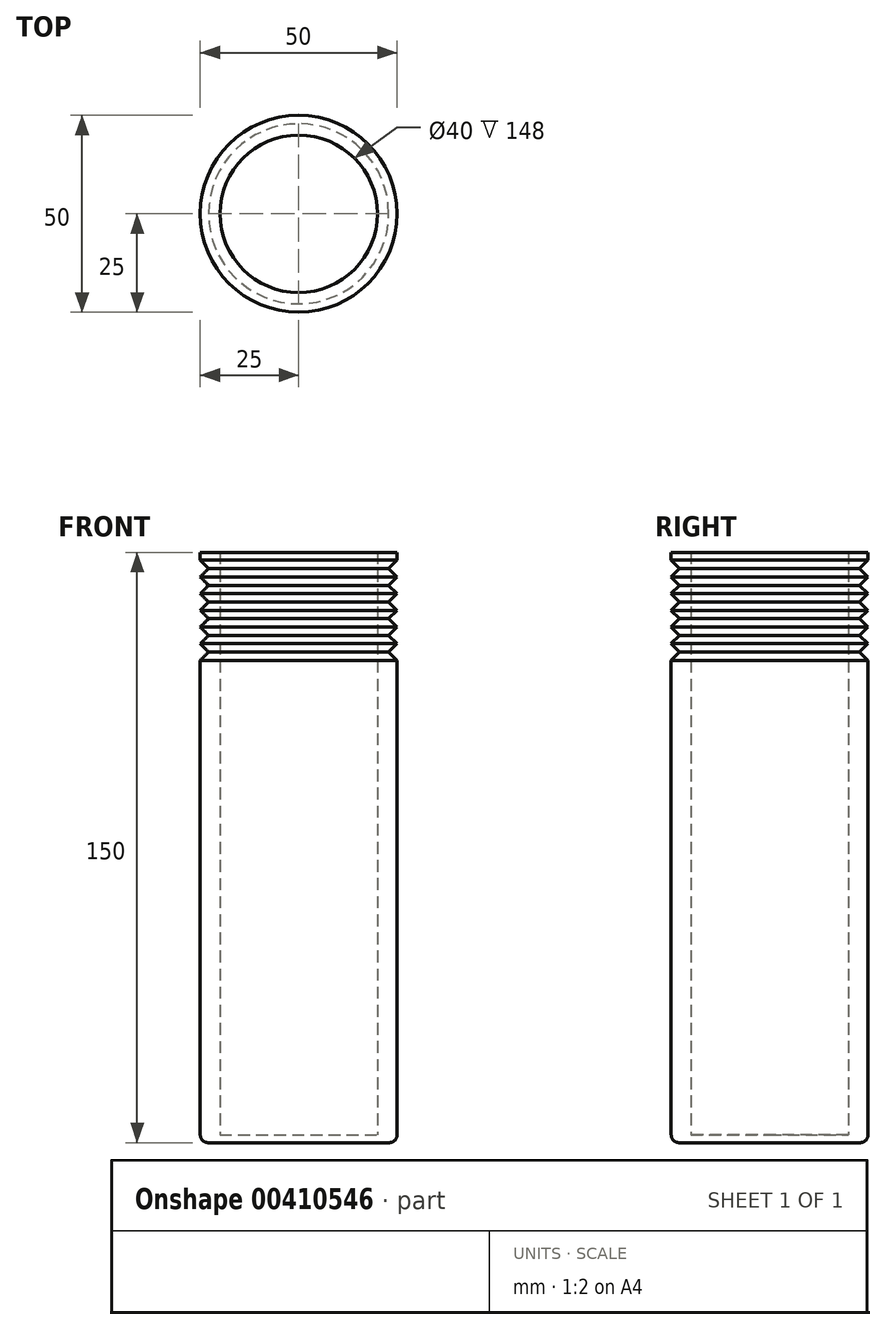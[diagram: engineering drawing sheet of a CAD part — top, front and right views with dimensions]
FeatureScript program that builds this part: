
annotation { "Feature Type Name" : "Feature", "Feature Type Description" : "" }
export const myFeature = defineFeature(function(context is Context, id is Id, definition is map)
    precondition{}
    {
        {
            var Q0;
            Q0=qCreatedBy(makeId("Front.planeOp"),FACE);
            var sketch = newSketch(context, id + "F0", { "sketchPlane" : qUnion([Q0])});
            skLineSegment(sketch, "E0", {"start": v(0, 0) * mm, "end": v(25, 0) * mm});
            skLineSegment(sketch, "E1", {"start": v(25, 0) * mm, "end": v(25, 122.52) * mm});
            skLineSegment(sketch, "E2", {"start": v(25, 150) * mm, "end": v(20, 150) * mm});
            skLineSegment(sketch, "E3", {"start": v(20, 150) * mm, "end": v(20, 2) * mm});
            skLineSegment(sketch, "E4", {"start": v(20, 2) * mm, "end": v(0, 2) * mm});
            skLineSegment(sketch, "E5", {"start": v(0, 2) * mm, "end": v(0, 0) * mm});
            skLineSegment(sketch, "E6", {"start": v(0, 2) * mm, "end": v(0, 245.04) * mm, "construction": true});
            skLineSegment(sketch, "E7", {"start": v(25, 147.98) * mm, "end": v(22.88, 145.86) * mm});
            skLineSegment(sketch, "E8", {"start": v(22.88, 145.86) * mm, "end": v(25, 143.74) * mm});
            skLineSegment(sketch, "E9", {"start": v(25, 143.74) * mm, "end": v(22.88, 141.62) * mm});
            skLineSegment(sketch, "E10", {"start": v(22.88, 141.62) * mm, "end": v(25, 139.5) * mm});
            skLineSegment(sketch, "E11", {"start": v(25, 139.5) * mm, "end": v(22.88, 137.37) * mm});
            skLineSegment(sketch, "E12", {"start": v(22.88, 137.37) * mm, "end": v(25, 135.25) * mm});
            skLineSegment(sketch, "E13", {"start": v(25, 135.25) * mm, "end": v(22.88, 133.13) * mm});
            skLineSegment(sketch, "E14", {"start": v(22.88, 133.13) * mm, "end": v(25, 131) * mm});
            skLineSegment(sketch, "E15", {"start": v(25, 131) * mm, "end": v(22.88, 128.89) * mm});
            skLineSegment(sketch, "E16", {"start": v(22.88, 128.89) * mm, "end": v(25, 126.77) * mm});
            skLineSegment(sketch, "E17", {"start": v(25, 126.77) * mm, "end": v(22.88, 124.64) * mm});
            skLineSegment(sketch, "E18", {"start": v(22.88, 124.64) * mm, "end": v(25, 122.52) * mm});
            skLineSegment(sketch, "E19.trimOffspring", {"start": v(25, 147.98) * mm, "end": v(25, 150) * mm});
            skSolve(sketch);
        }
        {
            var Q0;
            Q0 = qSketchRegion(id + "F0", true);
            var Q1;
            Q1=sQuery(id+"F0.wireOp",EDGE,"E6");
            revolve(context, id + "F1", {"entities" : qUnion([Q0]), "axis" : qUnion([Q1]), "revolveType" : RevolveType.FULL});
        }
        {
            var Q0;
            Q0=makeQuery(id+"F1.opRevolve","SWEPT_EDGE",EDGE,{"disambiguationData":[OSD([sQuery(id+"F0.wireOp",EDGE,"E0"),sQuery(id+"F0.wireOp",EDGE,"E1")])]});
            fillet(context, id + "F2", {"entities" : qUnion([Q0]), "radius" : 2 * mm, "tangentPropagation" : true, "allowEdgeOverflow" : false});
        }
    });
